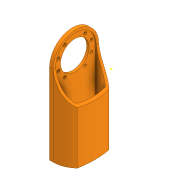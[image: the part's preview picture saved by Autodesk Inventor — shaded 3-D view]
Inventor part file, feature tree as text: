
AUTODESK INVENTOR PART (.ipt)
format: ipt  version: 2020 (Build 240168000, 168)  size: 203,776 bytes
history: native  units: in
note: dims shown in document units (in); Inventor stores cm internally (conversion verified against a paired STEP export)
features: sketch x6, extrude x4, projected_geometry x1
ambient origin geometry x8: Origin, YZ Plane, XZ Plane, XY Plane, X Axis, Y Axis, Z Axis, Center Point
bodies: Solid1 (feature_tree)
feature tree (11):
  extrude  "Extrusion1"  Depth=0.2362in
  sketch  "Sketch2"  dims[d6=0.2362in d7=0.2362in]
  extrude  "Extrusion2"  Depth=0.2362in
  sketch  "Sketch4"  dims[d10=0.2362in d11=0.2362in]
  extrude  "Extrusion3"  Depth=0.2362in
  extrude  "Extrusion4"  Depth=0.2362in
  sketch  "Sketch1"  dims[d3=2.3622in d5=0.2362in]
  sketch  "Sketch3"  dims[d8=0.2362in d9=0.2362in]
  sketch  "Sketch5"  dims[d12=0.2362in]
  sketch  "Sketch6"  dims[d13=4.85in d14=0.1969in d15=0.0in d16=0.0394in d17=0.0394in d18=0.1969in d19=0.1969in d20=0.0787in d21=0.0in d22=1.7717in d23=1.2598in d24=2.5197in d25=0.1181in d26=0.1969in d27=6.4173in d28=0.0in d29=1.1811in d30=6.4173in d31=0.0in]
  projected_geometry  "Projected Loop1"
